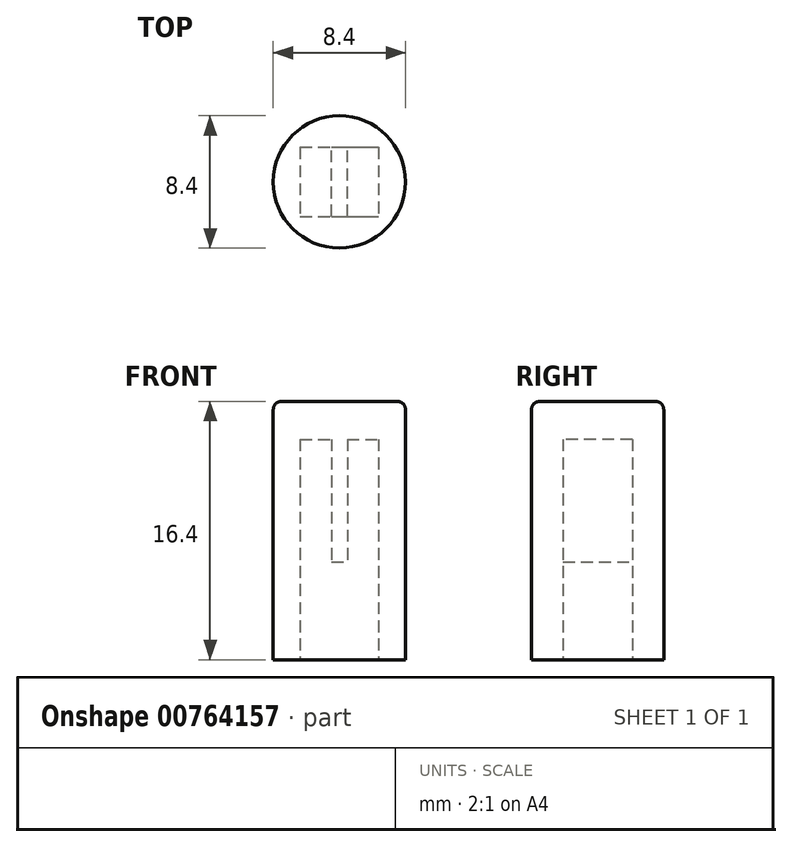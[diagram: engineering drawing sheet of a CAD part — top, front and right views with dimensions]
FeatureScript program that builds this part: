
annotation { "Feature Type Name" : "Feature", "Feature Type Description" : "" }
export const myFeature = defineFeature(function(context is Context, id is Id, definition is map)
    precondition{}
    {
        {
            var Q0;
            Q0=qCreatedBy(makeId("Top.planeOp"),FACE);
            var sketch = newSketch(context, id + "F0", { "sketchPlane" : qUnion([Q0])});
            skCircle(sketch, "E0", {"center": v(0, 0) * mm, "radius": 4.2 * mm});
            skLineSegment(sketch, "E1.bottom", {"start": v(-2.5, 2.2) * mm, "end": v(2.5, 2.2) * mm});
            skLineSegment(sketch, "E1.top", {"start": v(-2.5, -2.2) * mm, "end": v(2.5, -2.2) * mm});
            skLineSegment(sketch, "E1.left", {"start": v(-2.5, 2.2) * mm, "end": v(-2.5, -2.2) * mm});
            skLineSegment(sketch, "E1.right", {"start": v(2.5, 2.2) * mm, "end": v(2.5, -2.2) * mm});
            skLineSegment(sketch, "E2", {"start": v(-0.5, 2.2) * mm, "end": v(-0.5, -2.2) * mm});
            skLineSegment(sketch, "E3", {"start": v(0.5, 2.2) * mm, "end": v(0.5, -2.2) * mm});
            skSolve(sketch);
        }
        {
            var Q0;
            Q0=makeQuery(id+"F0.imprint","IMPRINT",FACE,{"disambiguationData":[TD([[makeQuery(id+"F0.imprint","IMPRINT",EDGE,{"derivedFrom":sQuery(id+"F0.wireOp",EDGE,"E0")}),1.0]])]});
            var Q1;
            {var subQ0=sQuery(id+"F0.wireOp",EDGE,"E1.left");Q1=makeQuery(id+"F0.imprint","IMPRINT",FACE,{"disambiguationData":[TD([[makeQuery(id+"F0.imprint","IMPRINT",EDGE,{"derivedFrom":subQ0}),1.0]])]});}
            var Q2;
            {var subQ0=sQuery(id+"F0.wireOp",EDGE,"E1.right");Q2=makeQuery(id+"F0.imprint","IMPRINT",FACE,{"disambiguationData":[TD([[makeQuery(id+"F0.imprint","IMPRINT",EDGE,{"derivedFrom":subQ0}),-1.0]])]});}
            var Q3;
            {var subQ0=sQuery(id+"F0.wireOp",EDGE,"E2");Q3=makeQuery(id+"F0.imprint","IMPRINT",FACE,{"disambiguationData":[TD([[makeQuery(id+"F0.imprint","IMPRINT",EDGE,{"derivedFrom":subQ0}),1.0]])]});}
            extrude(context, id + "F1", {"entities" : qUnion([Q0, Q1, Q2, Q3]), "depth" : 16.4 * mm, "offsetDistance" : 25 * mm});
        }
        {
            var Q0;
            {var subQ0=sQuery(id+"F0.wireOp",EDGE,"E1.right");Q0=makeQuery(id+"F0.imprint","IMPRINT",FACE,{"disambiguationData":[TD([[makeQuery(id+"F0.imprint","IMPRINT",EDGE,{"derivedFrom":subQ0}),-1.0]])]});}
            var Q1;
            {var subQ0=sQuery(id+"F0.wireOp",EDGE,"E1.left");Q1=makeQuery(id+"F0.imprint","IMPRINT",FACE,{"disambiguationData":[TD([[makeQuery(id+"F0.imprint","IMPRINT",EDGE,{"derivedFrom":subQ0}),1.0]])]});}
            var Q2;
            {var subQ0=sQuery(id+"F0.wireOp",EDGE,"E2");Q2=makeQuery(id+"F0.imprint","IMPRINT",FACE,{"disambiguationData":[TD([[makeQuery(id+"F0.imprint","IMPRINT",EDGE,{"derivedFrom":subQ0}),1.0]])]});}
            extrude(context, id + "F2", {"entities" : qUnion([Q0, Q1, Q2]), "operationType" : NewBodyOperationType.REMOVE, "depth" : 6.2 * mm, "offsetDistance" : 25 * mm});
        }
        {
            var Q0;
            {var subQ0=sQuery(id+"F0.wireOp",EDGE,"E1.right");Q0=makeQuery(id+"F0.imprint","IMPRINT",FACE,{"disambiguationData":[TD([[makeQuery(id+"F0.imprint","IMPRINT",EDGE,{"derivedFrom":subQ0}),-1.0]])]});}
            var Q1;
            {var subQ0=sQuery(id+"F0.wireOp",EDGE,"E1.left");Q1=makeQuery(id+"F0.imprint","IMPRINT",FACE,{"disambiguationData":[TD([[makeQuery(id+"F0.imprint","IMPRINT",EDGE,{"derivedFrom":subQ0}),1.0]])]});}
            extrude(context, id + "F3", {"entities" : qUnion([Q0, Q1]), "operationType" : NewBodyOperationType.REMOVE, "depth" : 14 * mm, "offsetDistance" : 25 * mm});
        }
        {
            var Q0;
            Q0=makeQuery(id+"F1.opExtrude","CAP_EDGE",EDGE,{"disambiguationData":[OSD([sQuery(id+"F0.wireOp",EDGE,"E0")])],"isStart":false});
            fillet(context, id + "F4", {"entities" : qUnion([Q0]), "radius" : 0.5 * mm, "tangentPropagation" : true, "allowEdgeOverflow" : false});
        }
    });
